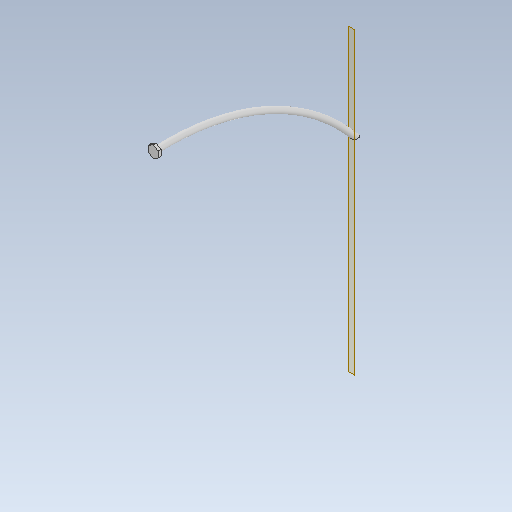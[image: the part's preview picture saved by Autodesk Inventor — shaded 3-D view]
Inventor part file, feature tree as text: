
AUTODESK INVENTOR PART (.ipt)
format: ipt  version: 2021 (Build 250183000, 183)  size: 229,376 bytes
history: native  units: mm
features: sketch x6, extrude x3, sweep x2, fillet x1, plane x1
ambient origin geometry x8: Origin, YZ Plane, XZ Plane, XY Plane, X Axis, Y Axis, Z Axis, Center Point
bodies: Solid1 (feature_tree)
feature tree (13):
  sketch  "Sketch1"  dims[d0=3300.0mm d1=1650.0mm]
  sweep  "Sweep1"
  sweep  "Sweep2"
  extrude  "Extrusion1"  Depth=30.0mm
  extrude  "Extrusion2"  Depth=1650.0mm
  fillet  "Fillet2"  [1 undecoded]
  plane  "Work Plane1"
  extrude  "Extrusion4"  Depth=3460.0mm
  sketch  "Sketch2"  dims[d2=0.0mm d3=40.0mm]
  sketch  "Sketch3"  dims[d4=0.0mm d5=0.0mm d6=30.0mm]
  sketch  "Sketch4"  dims[d7=0.0mm d8=1650.0mm d9=0.0mm d10=0.0mm]
  sketch  "Sketch5"  dims[d11=1810.0mm d12=3460.0mm]
  sketch  "Sketch6"  dims[d13=1730.0mm d14=1050.0mm d15=1730.0mm d16=1730.0mm d17=80.0mm d18=80.0mm d19=0.0mm d20=5.0mm d21=2.5mm d22=5.0mm d23=0.0mm d25=2.0mm d26=-1250.0mm d32=120.0deg d33=120.0deg d34=40.0mm d35=120.0deg d36=120.0deg d37=120.0deg d38=20.0mm d39=0.0mm]
note: 1 required parameter value undecoded (feature->parameter linkage not recoverable at this tier; creation-order binding heuristic only, values carry confidence <= 0.55)
